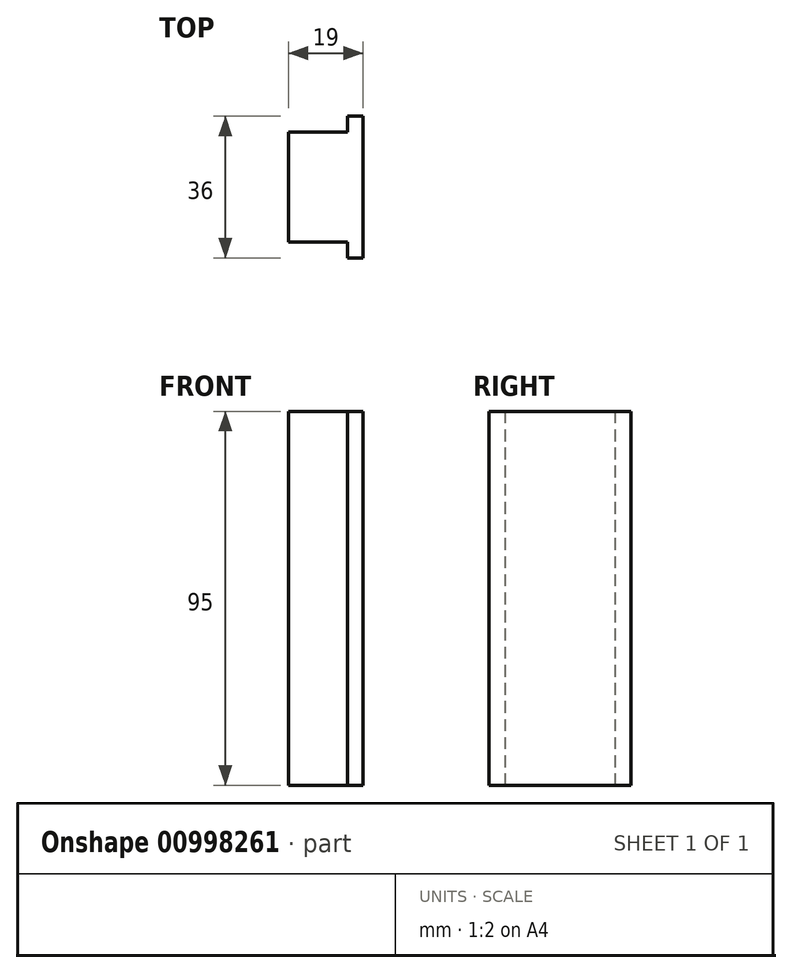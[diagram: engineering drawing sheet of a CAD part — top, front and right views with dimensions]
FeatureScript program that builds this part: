
annotation { "Feature Type Name" : "Feature", "Feature Type Description" : "" }
export const myFeature = defineFeature(function(context is Context, id is Id, definition is map)
    precondition{}
    {
        {
            var Q0;
            Q0=qCreatedBy(makeId("Top.planeOp"),FACE);
            var sketch = newSketch(context, id + "F0", { "sketchPlane" : qUnion([Q0])});
            skLineSegment(sketch, "E0.bottom", {"start": v(2, 18) * mm, "end": v(-2, 18) * mm});
            skLineSegment(sketch, "E0.top", {"start": v(2, -18) * mm, "end": v(-2, -18) * mm});
            skLineSegment(sketch, "E0.left", {"start": v(2, 18) * mm, "end": v(2, -18) * mm});
            skLineSegment(sketch, "E0.right", {"start": v(-2, 18) * mm, "end": v(-2, -18) * mm});
            skPoint(sketch, "E0.middle", {"position": v(0, 0) * mm});
            skLineSegment(sketch, "E1.bottom", {"start": v(-17, 9) * mm, "end": v(-2, 9) * mm});
            skLineSegment(sketch, "E1.top", {"start": v(-17, -9) * mm, "end": v(-2, -9) * mm});
            skLineSegment(sketch, "E1.left", {"start": v(-17, 9) * mm, "end": v(-17, -9) * mm});
            skPoint(sketch, "E1.middle", {"position": v(-2, 0) * mm});
            skLineSegment(sketch, "E2", {"start": v(-17, 9) * mm, "end": v(-17, 14) * mm});
            skLineSegment(sketch, "E3", {"start": v(-17, 14) * mm, "end": v(-2, 14) * mm});
            skLineSegment(sketch, "E4", {"start": v(-17, -9) * mm, "end": v(-17, -14) * mm});
            skLineSegment(sketch, "E5", {"start": v(-17, -14) * mm, "end": v(-2, -14) * mm});
            skSolve(sketch);
        }
        {
            var Q0;
            Q0=qSketchRegion(id+"F0",true);
            extrude(context, id + "F1", {"entities" : qUnion([Q0]), "depth" : 95 * mm, "offsetDistance" : 25 * mm});
        }
    });
